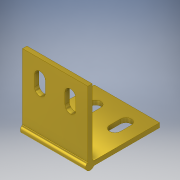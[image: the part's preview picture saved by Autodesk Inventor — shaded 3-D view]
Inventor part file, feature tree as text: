
AUTODESK INVENTOR PART (.ipt)
format: ipt  version: 2018 (Build 220112000, 112)  size: 173,056 bytes
history: native  units: in
note: dims shown in document units (in); Inventor stores cm internally (conversion verified against a paired STEP export)
features: projected_geometry x5, extrude x3, sketch x3
ambient origin geometry x8: Origin, YZ Plane, XZ Plane, XY Plane, X Axis, Y Axis, Z Axis, Center Point
bodies: Solid1 (feature_tree)
feature tree (11):
  extrude  "Extrusion1"  Depth=0.0787in
  extrude  "Extrusion2"  Depth=1.1811in TaperAngle=0.0deg
  extrude  "Extrusion3"  Depth=0.3937in
  sketch  "Sketch1"  dims[d6=0.0787in d8=1.1917in]
  sketch  "Sketch2"  dims[d9=1.1917in d10=1.1811in d11=0.0in]
  sketch  "Sketch3"  dims[d12=0.1969in d13=0.3937in d14=0.1969in d15=0.3937in d16=0.3937in d17=0.3937in d18=0.315in d19=0.315in d20=0.3937in d21=0.0in d23=0.3937in d24=0.1969in d25=0.3937in d26=0.315in d27=0.3937in d28=0.1969in d29=0.315in d30=0.3937in d31=0.3937in d32=0.0in d33=0.0787in]
  projected_geometry  "Projected Loop1"
  projected_geometry  "Projected Loop2"
  projected_geometry  "Projected Loop3"
  projected_geometry  "Projected Loop4"
  projected_geometry  "Projected Loop5"
